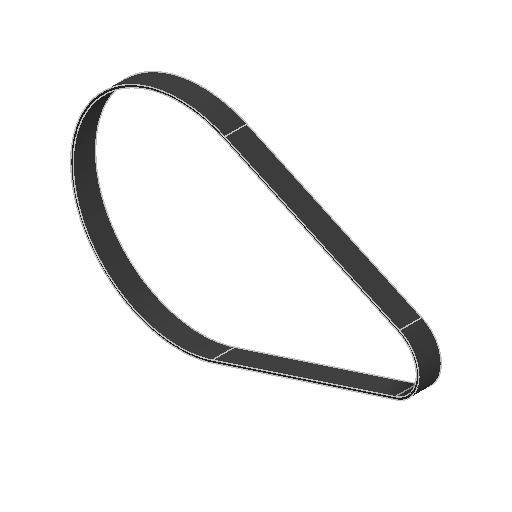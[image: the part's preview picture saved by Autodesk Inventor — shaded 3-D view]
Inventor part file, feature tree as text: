
AUTODESK INVENTOR PART (.ipt)
format: ipt  version: 2025.2 (Build 292293000, 293)  size: 110,080 bytes
history: native  units: in
note: dims shown in document units (in); Inventor stores cm internally (conversion verified against a paired STEP export)
features: extrude x1, sketch x1
ambient origin geometry x8: Origin, YZ Plane, XZ Plane, XY Plane, X Axis, Y Axis, Z Axis, Center Point
bodies: Solid1 (feature_tree)
feature tree (2):
  extrude  "Extrusion1"  Depth=0.358in
  sketch  "Sketch1"  dims[d0=3.388in d1=0.984in d2=3.3in d3=3.468in d4=1.064in d5=0.04in d6=0.04in d7=0.358in d8=0.0in]
